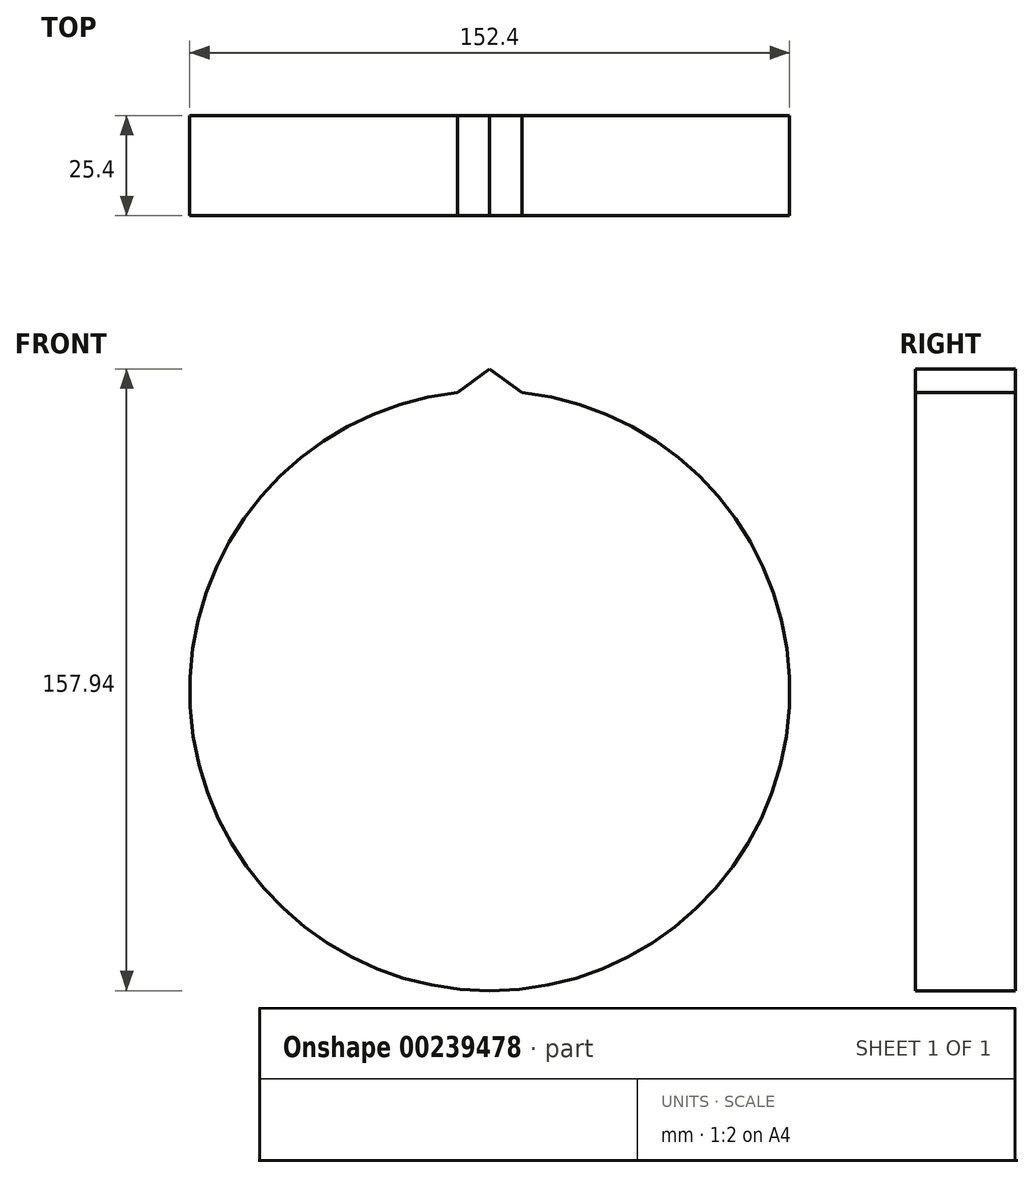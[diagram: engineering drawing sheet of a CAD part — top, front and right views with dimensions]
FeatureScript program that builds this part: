
annotation { "Feature Type Name" : "Feature", "Feature Type Description" : "" }
export const myFeature = defineFeature(function(context is Context, id is Id, definition is map)
    precondition{}
    {
        {
            var Q0;
            Q0=qCreatedBy(makeId("Front.planeOp"),FACE);
            var sketch = newSketch(context, id + "F0", { "sketchPlane" : qUnion([Q0])});
            skCircle(sketch, "E0", {"center": v(0, 0) * mm, "radius": 76.2 * mm});
            skSolve(sketch);
        }
        {
            var Q0;
            Q0 = qSketchRegion(id + "F0", true);
            extrude(context, id + "F1", {"entities" : qUnion([Q0]), "depth" : 25.4 * mm});
        }
        {
            var Q0;
            Q0=makeQuery(id+"F1.opExtrude","CAP_FACE",FACE,{"disambiguationData":[OSD([sQuery(id+"F0.wireOp",EDGE,"E0")])],"isStart":false});
            var sketch = newSketch(context, id + "F2", { "sketchPlane" : qUnion([Q0])});
            skLineSegment(sketch, "E1", {"start": v(-8.2, 75.76) * mm, "end": v(0, 81.74) * mm});
            skLineSegment(sketch, "E2", {"start": v(0, 81.74) * mm, "end": v(8.2, 75.76) * mm});
            skSolve(sketch);
        }
        {
            var Q0;
            {var subQ0=sQuery(id+"F2.wireOp",EDGE,"E1");Q0=makeQuery(id+"F2.imprint","IMPRINT",FACE,{"disambiguationData":[TD([[makeQuery(id+"F2.imprint","IMPRINT",EDGE,{"derivedFrom":subQ0}),-1.0]])]});}
            extrude(context, id + "F3", {"entities" : qUnion([Q0]), "operationType" : NewBodyOperationType.ADD, "oppositeDirection" : true, "depth" : 25.4 * mm});
        }
    });
